# Revit family: LPKB Silent 160 B1 EC_7540648
name_source: partatom
category: Mechanical Equipment
revit_build: Autodesk Revit MEP 2014 (Build: 20130308_1515(x64)
units: mm (PartAtom-declared; Revit-internal decimal feet)

## types (1)
- LPKB Silent 160 B1 EC
    Capacitor = -
    Current = 1 A
    Depth = 390 mm  [stored 1.27953 ft]
    Description = SOUND ATTENUATED DUCT FANS WITH CIRCULAR CONNECTIONS
    Diameter = 160 mm  [stored 0.524934 ft]
    Distance 1 = 91 mm  [stored 0.298556 ft]
    Distance 2 = 220 mm
    Frequency = 50 Hz
    Height = 248 mm  [stored 0.813648 ft]
    Main Material = Steel, Galvanized
    Max. temperature of transported air = 60 °C
    Max. temperature of transported air when speed controlled = 60 °C
    Phase = 1
    Power = 118 W
    Radius = 80 mm  [stored 0.262467 ft]
    Sound pressure level at 3 m = 56
    Speed = 3650
    Vertical Distance = 142 mm
    Voltage = 230 V
    Voltage range = 200-240
    Weight = 8.00 kg
    Width = 457 mm  [stored 1.49934 ft]
    Width A = 361 mm
    Wiring diagram = 4040143

note: [stored X ft] marks values corroborated as IEEE doubles in the binary element streams (Revit-internal decimal feet)

## geometry (parser evidence)
native form markers: Sweep x6
no freeform markers — native parametric forms only
